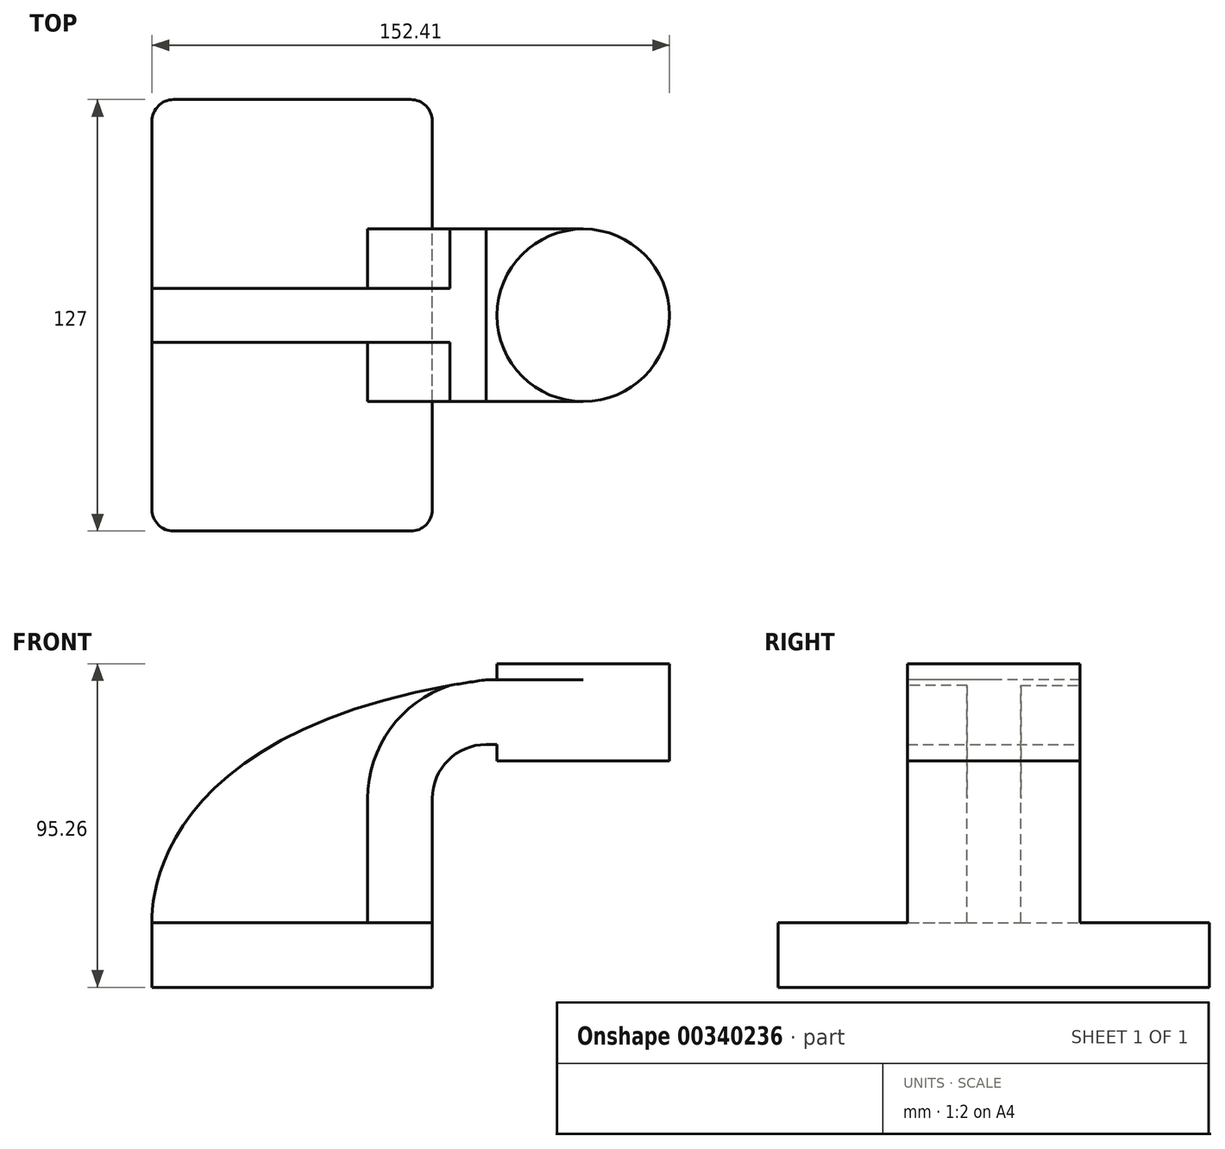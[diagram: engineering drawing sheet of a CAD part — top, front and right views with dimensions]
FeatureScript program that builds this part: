
annotation { "Feature Type Name" : "Feature", "Feature Type Description" : "" }
export const myFeature = defineFeature(function(context is Context, id is Id, definition is map)
    precondition{}
    {
        {
            var Q0;
            Q0=qCreatedBy(makeId("Front.planeOp"),FACE);
            var sketch = newSketch(context, id + "F0", { "sketchPlane" : qUnion([Q0])});
            skLineSegment(sketch, "E0.bottom", {"start": v(41.27, 9.53) * mm, "end": v(-41.28, 9.53) * mm});
            skLineSegment(sketch, "E0.top", {"start": v(41.28, -9.52) * mm, "end": v(-41.27, -9.52) * mm});
            skLineSegment(sketch, "E0.left", {"start": v(41.28, 9.53) * mm, "end": v(41.28, -9.52) * mm});
            skLineSegment(sketch, "E0.right", {"start": v(-41.28, 9.53) * mm, "end": v(-41.27, -9.52) * mm});
            skPoint(sketch, "E0.middle", {"position": v(0, 0) * mm});
            skLineSegment(sketch, "E1.bottom", {"start": v(60.32, 57.15) * mm, "end": v(111.12, 57.15) * mm});
            skLineSegment(sketch, "E1.top", {"start": v(60.32, 85.73) * mm, "end": v(111.12, 85.73) * mm});
            skLineSegment(sketch, "E1.left", {"start": v(60.32, 57.15) * mm, "end": v(60.32, 85.73) * mm});
            skLineSegment(sketch, "E1.right", {"start": v(111.12, 57.15) * mm, "end": v(111.12, 85.73) * mm});
            skPoint(sketch, "E1.middle", {"position": v(85.72, 71.44) * mm});
            skLineSegment(sketch, "E2", {"start": v(41.27, 9.53) * mm, "end": v(41.27, 46.05) * mm});
            skArc(sketch, "E3", {"start": v(41.27, 46.05) * mm, "mid": v(45.92, 57.28) * mm, "end": v(57.15, 61.93) * mm});
            skArc(sketch, "E4.1", {"start": v(22.22, 46.05) * mm, "mid": v(32.45, 70.75) * mm, "end": v(57.15, 80.98) * mm});
            skLineSegment(sketch, "E4.2", {"start": v(22.22, 9.53) * mm, "end": v(22.22, 46.05) * mm});
            skFitSpline(sketch, "E5", {"points": [v(-41.28, 9.52) * mm, v(57.15, 80.98) * mm], "startDerivative": vector(-0.93, 38.33) * mm, "endDerivative": vector(274.2, 37.56) * mm});
            skLineSegment(sketch, "E6", {"start": v(57.15, 61.93) * mm, "end": v(85.64, 61.93) * mm});
            skLineSegment(sketch, "E7", {"start": v(57.15, 80.98) * mm, "end": v(85.72, 80.98) * mm});
            skPoint(sketch, "E7.endSnap0", {"position": v(85.72, 85.73) * mm});
            skLineSegment(sketch, "E8", {"start": v(85.72, 57.15) * mm, "end": v(85.72, 85.73) * mm});
            skSolve(sketch);
        }
        {
            var Q0;
            Q0=makeQuery(id+"F0.imprint","IMPRINT",FACE,{"disambiguationData":[TD([[makeQuery(id+"F0.imprint","IMPRINT",EDGE,{"derivedFrom":sQuery(id+"F0.wireOp",EDGE,"E0.top")}),-1.0]])]});
            extrude(context, id + "F1", {"entities" : qUnion([Q0]), "endBound" : BoundingType.SYMMETRIC, "depth" : 127 * mm});
        }
        {
            var Q0;
            {var subQ6=sQuery(id+"F0.wireOp",EDGE,"E2");Q0=makeQuery(id+"F0.imprint","IMPRINT",FACE,{"disambiguationData":[TD([[makeQuery(id+"F0.imprint","IMPRINT",EDGE,{"derivedFrom":subQ6}),1.0]])]});}
            var Q1;
            {var subQ0=sQuery(id+"F0.wireOp",EDGE,"TVwEeYV9-Bfuo-ZEJT-o4jv-vEqjgyL6SaVX");var subQ1=sQuery(id+"F0.wireOp",EDGE,"E1.left");var subQ2=makeQuery(id+"F0.imprint","INTERSECT",VERTEX,{"derivedFrom":[subQ1,subQ0]});Q1=makeQuery(id+"F0.imprint","IMPRINT",FACE,{"disambiguationData":[TD([[makeQuery(id+"F0.imprint","IMPRINT",EDGE,{"disambiguationData":[TD([[subQ2,-1.0]])],"derivedFrom":subQ1}),-1.0]])]});}
            extrude(context, id + "F2", {"entities" : qUnion([Q0, Q1]), "operationType" : NewBodyOperationType.ADD, "endBound" : BoundingType.SYMMETRIC, "depth" : 50.8 * mm});
        }
        {
            var Q0;
            {var subQ3=sQuery(id+"F0.wireOp",EDGE,"E4.2");Q0=makeQuery(id+"F0.imprint","IMPRINT",FACE,{"disambiguationData":[TD([[makeQuery(id+"F0.imprint","IMPRINT",EDGE,{"derivedFrom":subQ3}),1.0]])]});}
            extrude(context, id + "F3", {"entities" : qUnion([Q0]), "operationType" : NewBodyOperationType.ADD, "endBound" : BoundingType.SYMMETRIC, "depth" : 15.88 * mm});
        }
        {
            var Q0;
            {var subQ0=sQuery(id+"F0.wireOp",EDGE,"E1.right");Q0=makeQuery(id+"F0.imprint","IMPRINT",FACE,{"disambiguationData":[TD([[makeQuery(id+"F0.imprint","IMPRINT",EDGE,{"derivedFrom":subQ0}),1.0]])]});}
            var Q1;
            Q1=sQuery(id+"F0.wireOp",EDGE,"E8");
            revolve(context, id + "F4", {"operationType" : NewBodyOperationType.ADD, "entities" : qUnion([Q0]), "axis" : qUnion([Q1]), "revolveType" : RevolveType.FULL});
        }
        {
            var Q0;
            Q0=makeQuery(id+"F1.opExtrude","CAP_EDGE",EDGE,{"disambiguationData":[OSD([sQuery(id+"F0.wireOp",EDGE,"E0.left")])],"isStart":false});
            var Q1;
            Q1=makeQuery(id+"F1.opExtrude","CAP_EDGE",EDGE,{"disambiguationData":[OSD([sQuery(id+"F0.wireOp",EDGE,"E0.right")])],"isStart":false});
            var Q2;
            Q2=makeQuery(id+"F1.opExtrude","CAP_EDGE",EDGE,{"disambiguationData":[OSD([sQuery(id+"F0.wireOp",EDGE,"E0.right")])],"isStart":true});
            var Q3;
            Q3=makeQuery(id+"F1.opExtrude","CAP_EDGE",EDGE,{"disambiguationData":[OSD([sQuery(id+"F0.wireOp",EDGE,"E0.left")])],"isStart":true});
            fillet(context, id + "F5", {"entities" : qUnion([Q0, Q1, Q2, Q3]), "radius" : 6.35 * mm, "tangentPropagation" : true, "allowEdgeOverflow" : false});
        }
    });
